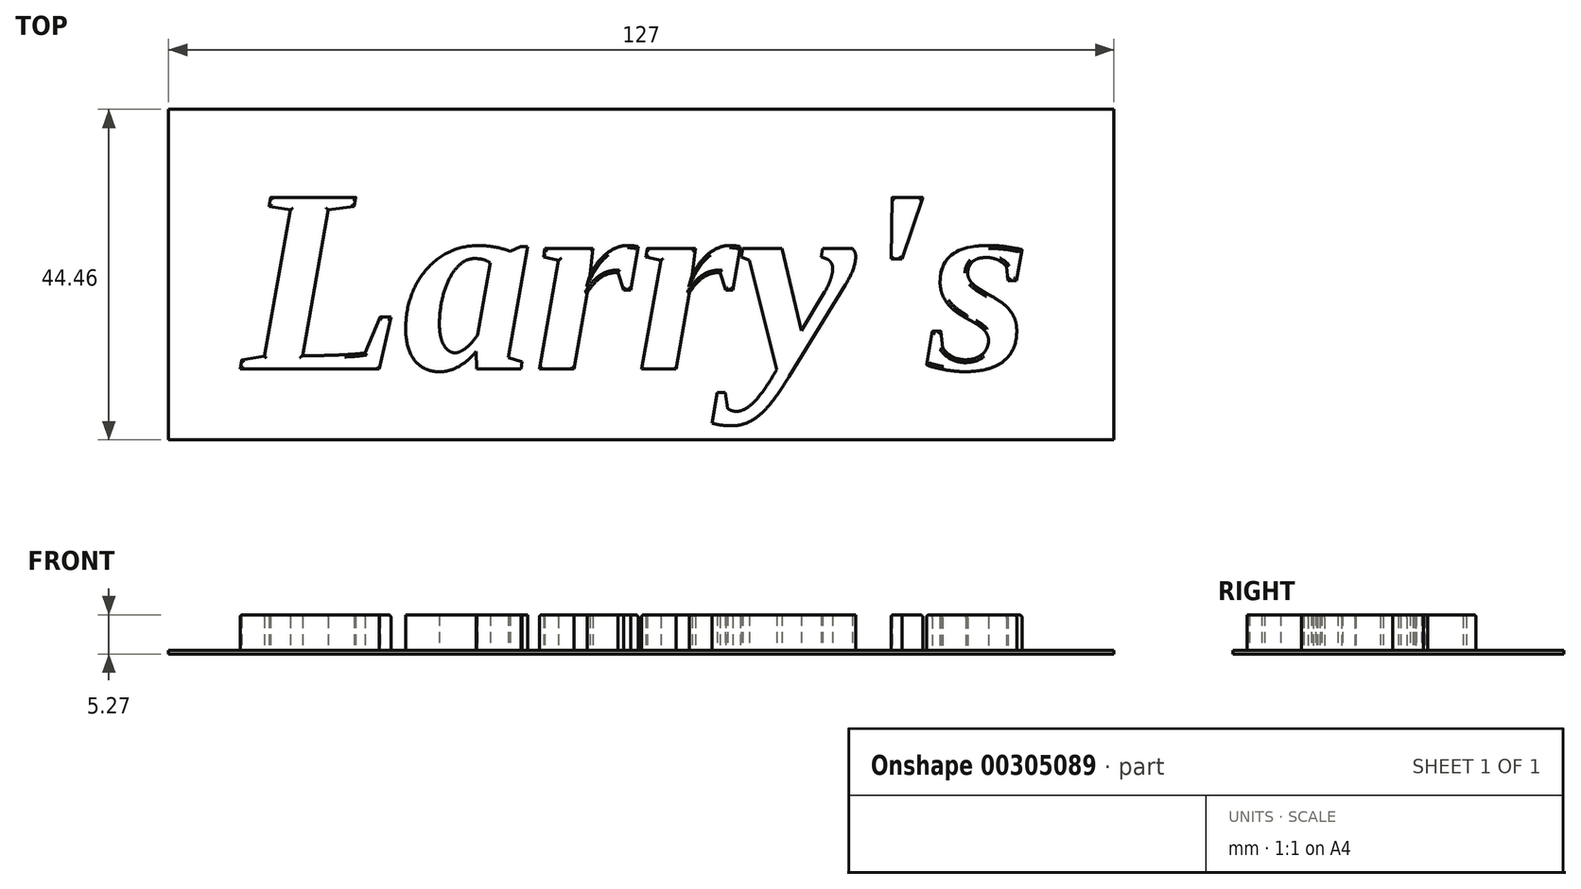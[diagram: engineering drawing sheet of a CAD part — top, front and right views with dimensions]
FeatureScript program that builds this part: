
annotation { "Feature Type Name" : "Feature", "Feature Type Description" : "" }
export const myFeature = defineFeature(function(context is Context, id is Id, definition is map)
    precondition{}
    {
        {
            var Q0;
            Q0=qCreatedBy(makeId("Top.planeOp"),FACE);
            var sketch = newSketch(context, id + "F0", { "sketchPlane" : qUnion([Q0])});
            skLineSegment(sketch, "E0.bottom", {"start": v(63.5, 22.23) * mm, "end": v(-63.5, 22.23) * mm});
            skLineSegment(sketch, "E0.top", {"start": v(63.5, -22.23) * mm, "end": v(-63.5, -22.23) * mm});
            skLineSegment(sketch, "E0.left", {"start": v(63.5, 22.23) * mm, "end": v(63.5, -22.22) * mm});
            skLineSegment(sketch, "E0.right", {"start": v(-63.5, 22.23) * mm, "end": v(-63.5, -22.23) * mm});
            skPoint(sketch, "E0.middle", {"position": v(0, 0) * mm});
            skSolve(sketch);
        }
        {
            var Q0;
            Q0 = qSketchRegion(id + "F2", true);
            var Q1;
            Q1 = qSketchRegion(id + "F0", true);
            extrude(context, id + "F1", {"entities" : qUnion([Q0, Q1]), "depth" : 0.5 * mm});
        }
        {
            var Q0;
            Q0=makeQuery(id+"F1.opExtrude","CAP_FACE",FACE,{"disambiguationData":[OSD([sQuery(id+"F0.wireOp",EDGE,"E0.bottom"),sQuery(id+"F0.wireOp",EDGE,"E0.top"),sQuery(id+"F0.wireOp",EDGE,"E0.left"),sQuery(id+"F0.wireOp",EDGE,"E0.right")])],"isStart":false});
            var sketch = newSketch(context, id + "F2", { "sketchPlane" : qUnion([Q0])});
            skText(sketch, "E1", { "text": "Larry\'s", "fontName": "Tinos-BoldItalic.ttf"});
            const initialGuessF2  = {"E1": [-0.0536, -0.0127, 1, 0, 0.0254]};
            skSetInitialGuess(sketch, initialGuessF2);
            skSolve(sketch);
        }
        {
            var Q0;
            Q0 = qSketchRegion(id + "F2", true);
            extrude(context, id + "F3", {"entities" : qUnion([Q0]), "operationType" : NewBodyOperationType.ADD, "depth" : 4.76 * mm});
        }
        {
            var Q0;
            Q0=makeQuery(id+"F3.opExtrude","CAP_EDGE",EDGE,{"disambiguationData":[OSD([sQuery(id+"F2.wireOp",EDGE,"E1.sketch_text.stroke-135")])],"isStart":false});
            var Q1;
            Q1=makeQuery(id+"F3.opExtrude","CAP_EDGE",EDGE,{"disambiguationData":[OSD([sQuery(id+"F2.wireOp",EDGE,"E1.sketch_text.stroke-137")])],"isStart":false});
            var Q2;
            Q2=makeQuery(id+"F3.opExtrude","CAP_EDGE",EDGE,{"disambiguationData":[OSD([sQuery(id+"F2.wireOp",EDGE,"E1.sketch_text.stroke-136")])],"isStart":false});
            var Q3;
            Q3=makeQuery(id+"F3.opExtrude","CAP_EDGE",EDGE,{"disambiguationData":[OSD([sQuery(id+"F2.wireOp",EDGE,"E1.sketch_text.stroke-138")])],"isStart":false});
            var Q4;
            Q4=makeQuery(id+"F3.opExtrude","CAP_EDGE",EDGE,{"disambiguationData":[OSD([sQuery(id+"F2.wireOp",EDGE,"E1.sketch_text.stroke-143")])],"isStart":false});
            var Q5;
            Q5=makeQuery(id+"F3.opExtrude","CAP_EDGE",EDGE,{"disambiguationData":[OSD([sQuery(id+"F2.wireOp",EDGE,"E1.sketch_text.stroke-144")])],"isStart":false});
            var Q6;
            Q6=makeQuery(id+"F3.opExtrude","CAP_EDGE",EDGE,{"disambiguationData":[OSD([sQuery(id+"F2.wireOp",EDGE,"E1.sketch_text.stroke-121")])],"isStart":false});
            var Q7;
            Q7=makeQuery(id+"F3.opExtrude","CAP_EDGE",EDGE,{"disambiguationData":[OSD([sQuery(id+"F2.wireOp",EDGE,"E1.sketch_text.stroke-122")])],"isStart":false});
            var Q8;
            Q8=makeQuery(id+"F3.opExtrude","CAP_FACE",FACE,{"disambiguationData":[OSD([sQuery(id+"F2.wireOp",EDGE,"E1.sketch_text.stroke-117"),sQuery(id+"F2.wireOp",EDGE,"E1.sketch_text.stroke-118"),sQuery(id+"F2.wireOp",EDGE,"E1.sketch_text.stroke-119"),sQuery(id+"F2.wireOp",EDGE,"E1.sketch_text.stroke-120"),sQuery(id+"F2.wireOp",EDGE,"E1.sketch_text.stroke-121"),sQuery(id+"F2.wireOp",EDGE,"E1.sketch_text.stroke-122"),sQuery(id+"F2.wireOp",EDGE,"E1.sketch_text.stroke-123"),sQuery(id+"F2.wireOp",EDGE,"E1.sketch_text.stroke-124"),sQuery(id+"F2.wireOp",EDGE,"E1.sketch_text.stroke-125"),sQuery(id+"F2.wireOp",EDGE,"E1.sketch_text.stroke-126"),sQuery(id+"F2.wireOp",EDGE,"E1.sketch_text.stroke-127"),sQuery(id+"F2.wireOp",EDGE,"E1.sketch_text.stroke-128"),sQuery(id+"F2.wireOp",EDGE,"E1.sketch_text.stroke-129"),sQuery(id+"F2.wireOp",EDGE,"E1.sketch_text.stroke-130"),sQuery(id+"F2.wireOp",EDGE,"E1.sketch_text.stroke-131"),sQuery(id+"F2.wireOp",EDGE,"E1.sketch_text.stroke-132"),sQuery(id+"F2.wireOp",EDGE,"E1.sketch_text.stroke-133"),sQuery(id+"F2.wireOp",EDGE,"E1.sketch_text.stroke-134"),sQuery(id+"F2.wireOp",EDGE,"E1.sketch_text.stroke-135"),sQuery(id+"F2.wireOp",EDGE,"E1.sketch_text.stroke-136"),sQuery(id+"F2.wireOp",EDGE,"E1.sketch_text.stroke-137"),sQuery(id+"F2.wireOp",EDGE,"E1.sketch_text.stroke-138"),sQuery(id+"F2.wireOp",EDGE,"E1.sketch_text.stroke-139"),sQuery(id+"F2.wireOp",EDGE,"E1.sketch_text.stroke-140"),sQuery(id+"F2.wireOp",EDGE,"E1.sketch_text.stroke-141"),sQuery(id+"F2.wireOp",EDGE,"E1.sketch_text.stroke-142"),sQuery(id+"F2.wireOp",EDGE,"E1.sketch_text.stroke-143"),sQuery(id+"F2.wireOp",EDGE,"E1.sketch_text.stroke-144"),sQuery(id+"F2.wireOp",EDGE,"E1.sketch_text.stroke-145"),sQuery(id+"F2.wireOp",EDGE,"E1.sketch_text.stroke-146"),sQuery(id+"F2.wireOp",EDGE,"E1.sketch_text.stroke-147"),sQuery(id+"F2.wireOp",EDGE,"E1.sketch_text.stroke-148"),sQuery(id+"F2.wireOp",EDGE,"E1.sketch_text.stroke-149"),sQuery(id+"F2.wireOp",EDGE,"E1.sketch_text.stroke-150"),sQuery(id+"F2.wireOp",EDGE,"E1.sketch_text.stroke-151"),sQuery(id+"F2.wireOp",EDGE,"E1.sketch_text.stroke-152"),sQuery(id+"F2.wireOp",EDGE,"E1.sketch_text.stroke-153"),sQuery(id+"F2.wireOp",EDGE,"E1.sketch_text.stroke-154"),sQuery(id+"F2.wireOp",EDGE,"E1.sketch_text.stroke-155"),sQuery(id+"F2.wireOp",EDGE,"E1.sketch_text.stroke-156"),sQuery(id+"F2.wireOp",EDGE,"E1.sketch_text.stroke-157"),sQuery(id+"F2.wireOp",EDGE,"E1.sketch_text.stroke-158"),sQuery(id+"F2.wireOp",EDGE,"E1.sketch_text.stroke-159"),sQuery(id+"F2.wireOp",EDGE,"E1.sketch_text.stroke-160"),sQuery(id+"F2.wireOp",EDGE,"E1.sketch_text.stroke-161"),sQuery(id+"F2.wireOp",EDGE,"E1.sketch_text.stroke-162"),sQuery(id+"F2.wireOp",EDGE,"E1.sketch_text.stroke-163"),sQuery(id+"F2.wireOp",EDGE,"E1.sketch_text.stroke-164"),sQuery(id+"F2.wireOp",EDGE,"E1.sketch_text.stroke-165"),sQuery(id+"F2.wireOp",EDGE,"E1.sketch_text.stroke-166"),sQuery(id+"F2.wireOp",EDGE,"E1.sketch_text.stroke-167"),sQuery(id+"F2.wireOp",EDGE,"E1.sketch_text.stroke-168"),sQuery(id+"F2.wireOp",EDGE,"E1.sketch_text.stroke-169"),sQuery(id+"F2.wireOp",EDGE,"E1.sketch_text.stroke-170"),sQuery(id+"F2.wireOp",EDGE,"E1.sketch_text.stroke-171"),sQuery(id+"F2.wireOp",EDGE,"E1.sketch_text.stroke-172"),sQuery(id+"F2.wireOp",EDGE,"E1.sketch_text.stroke-173"),sQuery(id+"F2.wireOp",EDGE,"E1.sketch_text.stroke-174"),sQuery(id+"F2.wireOp",EDGE,"E1.sketch_text.stroke-175"),sQuery(id+"F2.wireOp",EDGE,"E1.sketch_text.stroke-176"),sQuery(id+"F2.wireOp",EDGE,"E1.sketch_text.stroke-177"),sQuery(id+"F2.wireOp",EDGE,"E1.sketch_text.stroke-178"),sQuery(id+"F2.wireOp",EDGE,"E1.sketch_text.stroke-179"),sQuery(id+"F2.wireOp",EDGE,"E1.sketch_text.stroke-180"),sQuery(id+"F2.wireOp",EDGE,"E1.sketch_text.stroke-181"),sQuery(id+"F2.wireOp",EDGE,"E1.sketch_text.stroke-182"),sQuery(id+"F2.wireOp",EDGE,"E1.sketch_text.stroke-183"),sQuery(id+"F2.wireOp",EDGE,"E1.sketch_text.stroke-184"),sQuery(id+"F2.wireOp",EDGE,"E1.sketch_text.stroke-185"),sQuery(id+"F2.wireOp",EDGE,"E1.sketch_text.stroke-186"),sQuery(id+"F2.wireOp",EDGE,"E1.sketch_text.stroke-187"),sQuery(id+"F2.wireOp",EDGE,"E1.sketch_text.stroke-188"),sQuery(id+"F2.wireOp",EDGE,"E1.sketch_text.stroke-189")])],"isStart":false});
            var Q9;
            {var subQ0=sQuery(id+"F2.wireOp",EDGE,"E1.sketch_text.stroke-129");Q9=makeQuery(id+"F3.opExtrude","CAP_EDGE",EDGE,{"disambiguationData":[OSD([subQ0]),TDD([makeQuery(id+"F2.imprint","IMPRINT",EDGE,{"disambiguationData":[TD([[makeQuery(id+"F2.imprint","INTERSECT",VERTEX,{"derivedFrom":[subQ0,sQuery(id+"F2.wireOp",EDGE,"E1.sketch_text.stroke-130")]}),1.0]])],"derivedFrom":subQ0})])],"isStart":false});}
            fillet(context, id + "F4", {"entities" : qUnion([Q0, Q1, Q2, Q3, Q4, Q5, Q6, Q7, Q8, Q9]), "radius" : 0.38 * mm, "tangentPropagation" : true, "allowEdgeOverflow" : false});
        }
        {
            var Q0;
            Q0=makeQuery(id+"F3.opExtrude","CAP_FACE",FACE,{"disambiguationData":[OSD([sQuery(id+"F2.wireOp",EDGE,"E1.sketch_text.stroke-0"),sQuery(id+"F2.wireOp",EDGE,"E1.sketch_text.stroke-1"),sQuery(id+"F2.wireOp",EDGE,"E1.sketch_text.stroke-2"),sQuery(id+"F2.wireOp",EDGE,"E1.sketch_text.stroke-3"),sQuery(id+"F2.wireOp",EDGE,"E1.sketch_text.stroke-4"),sQuery(id+"F2.wireOp",EDGE,"E1.sketch_text.stroke-5"),sQuery(id+"F2.wireOp",EDGE,"E1.sketch_text.stroke-6"),sQuery(id+"F2.wireOp",EDGE,"E1.sketch_text.stroke-7"),sQuery(id+"F2.wireOp",EDGE,"E1.sketch_text.stroke-8"),sQuery(id+"F2.wireOp",EDGE,"E1.sketch_text.stroke-9"),sQuery(id+"F2.wireOp",EDGE,"E1.sketch_text.stroke-10"),sQuery(id+"F2.wireOp",EDGE,"E1.sketch_text.stroke-11"),sQuery(id+"F2.wireOp",EDGE,"E1.sketch_text.stroke-12"),sQuery(id+"F2.wireOp",EDGE,"E1.sketch_text.stroke-13"),sQuery(id+"F2.wireOp",EDGE,"E1.sketch_text.stroke-14"),sQuery(id+"F2.wireOp",EDGE,"E1.sketch_text.stroke-15"),sQuery(id+"F2.wireOp",EDGE,"E1.sketch_text.stroke-16"),sQuery(id+"F2.wireOp",EDGE,"E1.sketch_text.stroke-17"),sQuery(id+"F2.wireOp",EDGE,"E1.sketch_text.stroke-18"),sQuery(id+"F2.wireOp",EDGE,"E1.sketch_text.stroke-19"),sQuery(id+"F2.wireOp",EDGE,"E1.sketch_text.stroke-20"),sQuery(id+"F2.wireOp",EDGE,"E1.sketch_text.stroke-21"),sQuery(id+"F2.wireOp",EDGE,"E1.sketch_text.stroke-22"),sQuery(id+"F2.wireOp",EDGE,"E1.sketch_text.stroke-23"),sQuery(id+"F2.wireOp",EDGE,"E1.sketch_text.stroke-24"),sQuery(id+"F2.wireOp",EDGE,"E1.sketch_text.stroke-25"),sQuery(id+"F2.wireOp",EDGE,"E1.sketch_text.stroke-26"),sQuery(id+"F2.wireOp",EDGE,"E1.sketch_text.stroke-27"),sQuery(id+"F2.wireOp",EDGE,"E1.sketch_text.stroke-28"),sQuery(id+"F2.wireOp",EDGE,"E1.sketch_text.stroke-29"),sQuery(id+"F2.wireOp",EDGE,"E1.sketch_text.stroke-30")])],"isStart":false});
            var Q1;
            Q1=makeQuery(id+"F3.opExtrude","CAP_FACE",FACE,{"disambiguationData":[OSD([sQuery(id+"F2.wireOp",EDGE,"E1.sketch_text.stroke-31"),sQuery(id+"F2.wireOp",EDGE,"E1.sketch_text.stroke-32"),sQuery(id+"F2.wireOp",EDGE,"E1.sketch_text.stroke-33"),sQuery(id+"F2.wireOp",EDGE,"E1.sketch_text.stroke-34"),sQuery(id+"F2.wireOp",EDGE,"E1.sketch_text.stroke-35"),sQuery(id+"F2.wireOp",EDGE,"E1.sketch_text.stroke-36"),sQuery(id+"F2.wireOp",EDGE,"E1.sketch_text.stroke-37"),sQuery(id+"F2.wireOp",EDGE,"E1.sketch_text.stroke-38"),sQuery(id+"F2.wireOp",EDGE,"E1.sketch_text.stroke-39"),sQuery(id+"F2.wireOp",EDGE,"E1.sketch_text.stroke-40"),sQuery(id+"F2.wireOp",EDGE,"E1.sketch_text.stroke-41"),sQuery(id+"F2.wireOp",EDGE,"E1.sketch_text.stroke-42"),sQuery(id+"F2.wireOp",EDGE,"E1.sketch_text.stroke-43"),sQuery(id+"F2.wireOp",EDGE,"E1.sketch_text.stroke-44"),sQuery(id+"F2.wireOp",EDGE,"E1.sketch_text.stroke-45"),sQuery(id+"F2.wireOp",EDGE,"E1.sketch_text.stroke-46"),sQuery(id+"F2.wireOp",EDGE,"E1.sketch_text.stroke-47"),sQuery(id+"F2.wireOp",EDGE,"E1.sketch_text.stroke-48"),sQuery(id+"F2.wireOp",EDGE,"E1.sketch_text.stroke-49"),sQuery(id+"F2.wireOp",EDGE,"E1.sketch_text.stroke-50"),sQuery(id+"F2.wireOp",EDGE,"E1.sketch_text.stroke-51"),sQuery(id+"F2.wireOp",EDGE,"E1.sketch_text.stroke-52"),sQuery(id+"F2.wireOp",EDGE,"E1.sketch_text.stroke-53"),sQuery(id+"F2.wireOp",EDGE,"E1.sketch_text.stroke-54"),sQuery(id+"F2.wireOp",EDGE,"E1.sketch_text.stroke-55"),sQuery(id+"F2.wireOp",EDGE,"E1.sketch_text.stroke-56"),sQuery(id+"F2.wireOp",EDGE,"E1.sketch_text.stroke-57"),sQuery(id+"F2.wireOp",EDGE,"E1.sketch_text.stroke-58"),sQuery(id+"F2.wireOp",EDGE,"E1.sketch_text.stroke-59"),sQuery(id+"F2.wireOp",EDGE,"E1.sketch_text.stroke-60"),sQuery(id+"F2.wireOp",EDGE,"E1.sketch_text.stroke-61"),sQuery(id+"F2.wireOp",EDGE,"E1.sketch_text.stroke-62"),sQuery(id+"F2.wireOp",EDGE,"E1.sketch_text.stroke-63"),sQuery(id+"F2.wireOp",EDGE,"E1.sketch_text.stroke-64"),sQuery(id+"F2.wireOp",EDGE,"E1.sketch_text.stroke-65"),sQuery(id+"F2.wireOp",EDGE,"E1.sketch_text.stroke-66"),sQuery(id+"F2.wireOp",EDGE,"E1.sketch_text.stroke-67"),sQuery(id+"F2.wireOp",EDGE,"E1.sketch_text.stroke-68"),sQuery(id+"F2.wireOp",EDGE,"E1.sketch_text.stroke-69"),sQuery(id+"F2.wireOp",EDGE,"E1.sketch_text.stroke-70"),sQuery(id+"F2.wireOp",EDGE,"E1.sketch_text.stroke-71"),sQuery(id+"F2.wireOp",EDGE,"E1.sketch_text.stroke-72"),sQuery(id+"F2.wireOp",EDGE,"E1.sketch_text.stroke-73"),sQuery(id+"F2.wireOp",EDGE,"E1.sketch_text.stroke-74"),sQuery(id+"F2.wireOp",EDGE,"E1.sketch_text.stroke-75"),sQuery(id+"F2.wireOp",EDGE,"E1.sketch_text.stroke-76"),sQuery(id+"F2.wireOp",EDGE,"E1.sketch_text.stroke-77"),sQuery(id+"F2.wireOp",EDGE,"E1.sketch_text.stroke-78"),sQuery(id+"F2.wireOp",EDGE,"E1.sketch_text.stroke-79"),sQuery(id+"F2.wireOp",EDGE,"E1.sketch_text.stroke-80"),sQuery(id+"F2.wireOp",EDGE,"E1.sketch_text.stroke-81"),sQuery(id+"F2.wireOp",EDGE,"E1.sketch_text.stroke-82"),sQuery(id+"F2.wireOp",EDGE,"E1.sketch_text.stroke-83"),sQuery(id+"F2.wireOp",EDGE,"E1.sketch_text.stroke-84"),sQuery(id+"F2.wireOp",EDGE,"E1.sketch_text.stroke-85"),sQuery(id+"F2.wireOp",EDGE,"E1.sketch_text.stroke-86")])],"isStart":false});
            var Q2;
            Q2=makeQuery(id+"F3.opExtrude","CAP_FACE",FACE,{"disambiguationData":[OSD([sQuery(id+"F2.wireOp",EDGE,"E1.sketch_text.stroke-87"),sQuery(id+"F2.wireOp",EDGE,"E1.sketch_text.stroke-88"),sQuery(id+"F2.wireOp",EDGE,"E1.sketch_text.stroke-89"),sQuery(id+"F2.wireOp",EDGE,"E1.sketch_text.stroke-90"),sQuery(id+"F2.wireOp",EDGE,"E1.sketch_text.stroke-91"),sQuery(id+"F2.wireOp",EDGE,"E1.sketch_text.stroke-92"),sQuery(id+"F2.wireOp",EDGE,"E1.sketch_text.stroke-93"),sQuery(id+"F2.wireOp",EDGE,"E1.sketch_text.stroke-94"),sQuery(id+"F2.wireOp",EDGE,"E1.sketch_text.stroke-95"),sQuery(id+"F2.wireOp",EDGE,"E1.sketch_text.stroke-96"),sQuery(id+"F2.wireOp",EDGE,"E1.sketch_text.stroke-97"),sQuery(id+"F2.wireOp",EDGE,"E1.sketch_text.stroke-98"),sQuery(id+"F2.wireOp",EDGE,"E1.sketch_text.stroke-99"),sQuery(id+"F2.wireOp",EDGE,"E1.sketch_text.stroke-100"),sQuery(id+"F2.wireOp",EDGE,"E1.sketch_text.stroke-101"),sQuery(id+"F2.wireOp",EDGE,"E1.sketch_text.stroke-102"),sQuery(id+"F2.wireOp",EDGE,"E1.sketch_text.stroke-103"),sQuery(id+"F2.wireOp",EDGE,"E1.sketch_text.stroke-104"),sQuery(id+"F2.wireOp",EDGE,"E1.sketch_text.stroke-105"),sQuery(id+"F2.wireOp",EDGE,"E1.sketch_text.stroke-106"),sQuery(id+"F2.wireOp",EDGE,"E1.sketch_text.stroke-107"),sQuery(id+"F2.wireOp",EDGE,"E1.sketch_text.stroke-108"),sQuery(id+"F2.wireOp",EDGE,"E1.sketch_text.stroke-109"),sQuery(id+"F2.wireOp",EDGE,"E1.sketch_text.stroke-110"),sQuery(id+"F2.wireOp",EDGE,"E1.sketch_text.stroke-111"),sQuery(id+"F2.wireOp",EDGE,"E1.sketch_text.stroke-112"),sQuery(id+"F2.wireOp",EDGE,"E1.sketch_text.stroke-113"),sQuery(id+"F2.wireOp",EDGE,"E1.sketch_text.stroke-114"),sQuery(id+"F2.wireOp",EDGE,"E1.sketch_text.stroke-115"),sQuery(id+"F2.wireOp",EDGE,"E1.sketch_text.stroke-116")])],"isStart":false});
            var Q3;
            Q3=makeQuery(id+"F3.opExtrude","CAP_FACE",FACE,{"disambiguationData":[OSD([sQuery(id+"F2.wireOp",EDGE,"E1.sketch_text.stroke-194"),sQuery(id+"F2.wireOp",EDGE,"E1.sketch_text.stroke-195"),sQuery(id+"F2.wireOp",EDGE,"E1.sketch_text.stroke-196"),sQuery(id+"F2.wireOp",EDGE,"E1.sketch_text.stroke-197"),sQuery(id+"F2.wireOp",EDGE,"E1.sketch_text.stroke-198"),sQuery(id+"F2.wireOp",EDGE,"E1.sketch_text.stroke-199"),sQuery(id+"F2.wireOp",EDGE,"E1.sketch_text.stroke-200"),sQuery(id+"F2.wireOp",EDGE,"E1.sketch_text.stroke-201"),sQuery(id+"F2.wireOp",EDGE,"E1.sketch_text.stroke-202"),sQuery(id+"F2.wireOp",EDGE,"E1.sketch_text.stroke-203"),sQuery(id+"F2.wireOp",EDGE,"E1.sketch_text.stroke-204"),sQuery(id+"F2.wireOp",EDGE,"E1.sketch_text.stroke-205"),sQuery(id+"F2.wireOp",EDGE,"E1.sketch_text.stroke-206"),sQuery(id+"F2.wireOp",EDGE,"E1.sketch_text.stroke-207"),sQuery(id+"F2.wireOp",EDGE,"E1.sketch_text.stroke-208"),sQuery(id+"F2.wireOp",EDGE,"E1.sketch_text.stroke-209"),sQuery(id+"F2.wireOp",EDGE,"E1.sketch_text.stroke-210"),sQuery(id+"F2.wireOp",EDGE,"E1.sketch_text.stroke-211"),sQuery(id+"F2.wireOp",EDGE,"E1.sketch_text.stroke-212"),sQuery(id+"F2.wireOp",EDGE,"E1.sketch_text.stroke-213"),sQuery(id+"F2.wireOp",EDGE,"E1.sketch_text.stroke-214"),sQuery(id+"F2.wireOp",EDGE,"E1.sketch_text.stroke-215"),sQuery(id+"F2.wireOp",EDGE,"E1.sketch_text.stroke-216"),sQuery(id+"F2.wireOp",EDGE,"E1.sketch_text.stroke-217"),sQuery(id+"F2.wireOp",EDGE,"E1.sketch_text.stroke-218"),sQuery(id+"F2.wireOp",EDGE,"E1.sketch_text.stroke-219"),sQuery(id+"F2.wireOp",EDGE,"E1.sketch_text.stroke-220"),sQuery(id+"F2.wireOp",EDGE,"E1.sketch_text.stroke-221"),sQuery(id+"F2.wireOp",EDGE,"E1.sketch_text.stroke-222"),sQuery(id+"F2.wireOp",EDGE,"E1.sketch_text.stroke-223"),sQuery(id+"F2.wireOp",EDGE,"E1.sketch_text.stroke-224"),sQuery(id+"F2.wireOp",EDGE,"E1.sketch_text.stroke-225"),sQuery(id+"F2.wireOp",EDGE,"E1.sketch_text.stroke-226"),sQuery(id+"F2.wireOp",EDGE,"E1.sketch_text.stroke-227"),sQuery(id+"F2.wireOp",EDGE,"E1.sketch_text.stroke-228"),sQuery(id+"F2.wireOp",EDGE,"E1.sketch_text.stroke-229"),sQuery(id+"F2.wireOp",EDGE,"E1.sketch_text.stroke-230"),sQuery(id+"F2.wireOp",EDGE,"E1.sketch_text.stroke-231"),sQuery(id+"F2.wireOp",EDGE,"E1.sketch_text.stroke-232"),sQuery(id+"F2.wireOp",EDGE,"E1.sketch_text.stroke-233"),sQuery(id+"F2.wireOp",EDGE,"E1.sketch_text.stroke-234"),sQuery(id+"F2.wireOp",EDGE,"E1.sketch_text.stroke-235"),sQuery(id+"F2.wireOp",EDGE,"E1.sketch_text.stroke-236"),sQuery(id+"F2.wireOp",EDGE,"E1.sketch_text.stroke-237"),sQuery(id+"F2.wireOp",EDGE,"E1.sketch_text.stroke-238"),sQuery(id+"F2.wireOp",EDGE,"E1.sketch_text.stroke-239"),sQuery(id+"F2.wireOp",EDGE,"E1.sketch_text.stroke-240"),sQuery(id+"F2.wireOp",EDGE,"E1.sketch_text.stroke-241"),sQuery(id+"F2.wireOp",EDGE,"E1.sketch_text.stroke-242"),sQuery(id+"F2.wireOp",EDGE,"E1.sketch_text.stroke-243"),sQuery(id+"F2.wireOp",EDGE,"E1.sketch_text.stroke-244"),sQuery(id+"F2.wireOp",EDGE,"E1.sketch_text.stroke-245"),sQuery(id+"F2.wireOp",EDGE,"E1.sketch_text.stroke-246"),sQuery(id+"F2.wireOp",EDGE,"E1.sketch_text.stroke-247")])],"isStart":false});
            var Q4;
            Q4=makeQuery(id+"F3.opExtrude","CAP_FACE",FACE,{"disambiguationData":[OSD([sQuery(id+"F2.wireOp",EDGE,"E1.sketch_text.stroke-190"),sQuery(id+"F2.wireOp",EDGE,"E1.sketch_text.stroke-191"),sQuery(id+"F2.wireOp",EDGE,"E1.sketch_text.stroke-192"),sQuery(id+"F2.wireOp",EDGE,"E1.sketch_text.stroke-193")])],"isStart":false});
            fillet(context, id + "F5", {"entities" : qUnion([Q0, Q1, Q2, Q3, Q4]), "radius" : 0.3 * mm, "tangentPropagation" : true, "allowEdgeOverflow" : false});
        }
    });
